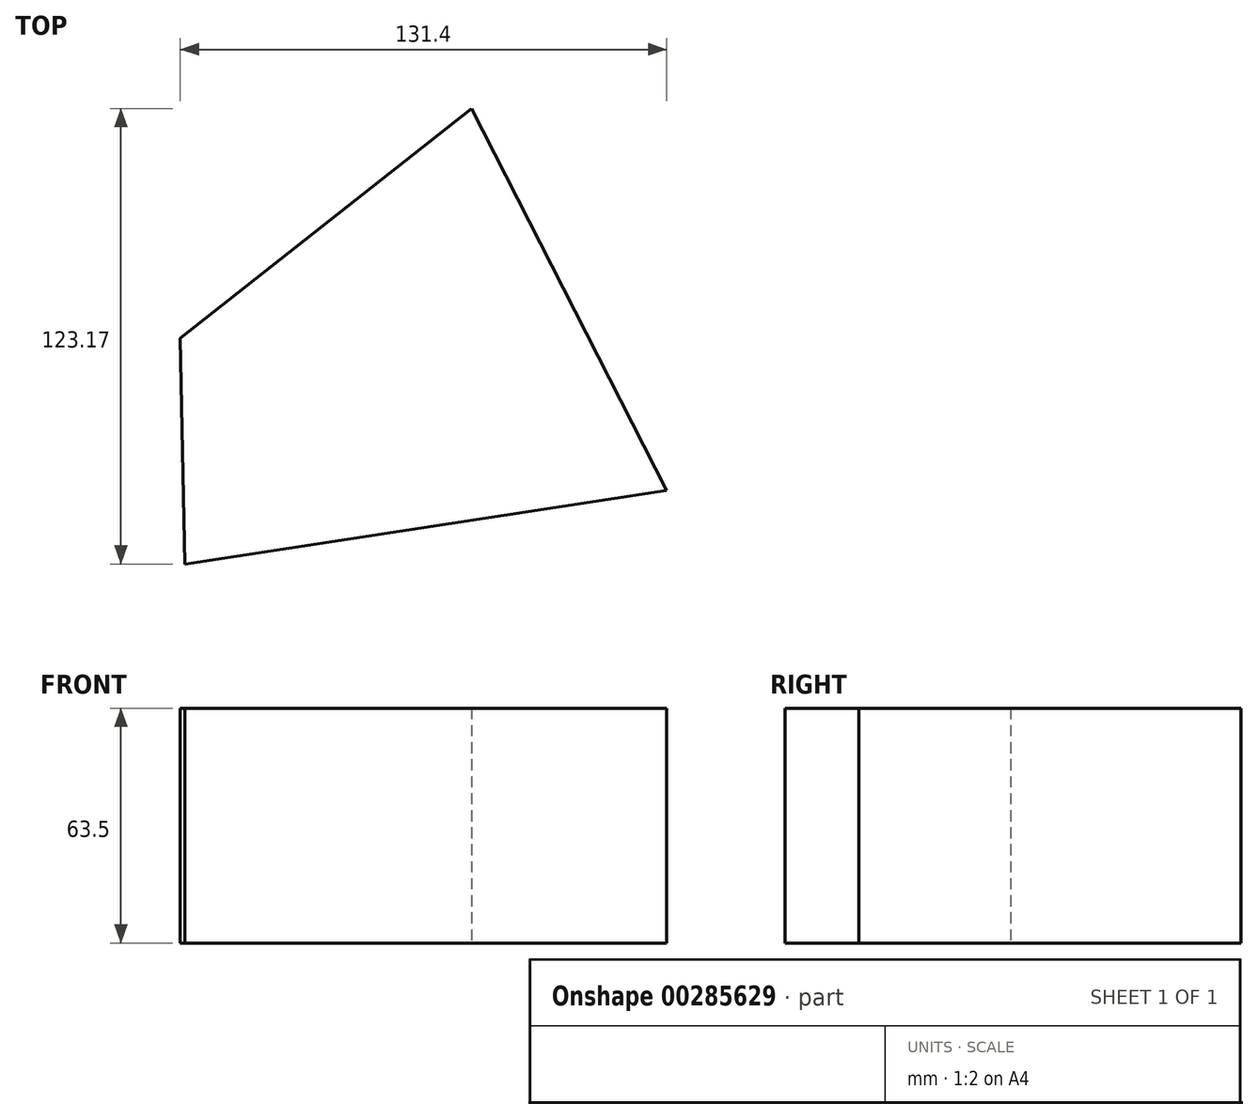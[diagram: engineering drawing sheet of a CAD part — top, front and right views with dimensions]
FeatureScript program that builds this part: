
annotation { "Feature Type Name" : "Feature", "Feature Type Description" : "" }
export const myFeature = defineFeature(function(context is Context, id is Id, definition is map)
    precondition{}
    {
        {
            var Q0;
            Q0=qCreatedBy(makeId("Top.planeOp"),FACE);
            var sketch = newSketch(context, id + "F0", { "sketchPlane" : qUnion([Q0])});
            skLineSegment(sketch, "E0", {"start": v(-57.79, -60.97) * mm, "end": v(72.36, -41.04) * mm});
            skLineSegment(sketch, "E1", {"start": v(72.36, -41.04) * mm, "end": v(19.66, 62.2) * mm});
            skLineSegment(sketch, "E2", {"start": v(19.66, 62.2) * mm, "end": v(-59.04, 0) * mm});
            skLineSegment(sketch, "E3", {"start": v(-57.79, -60.97) * mm, "end": v(-59.04, 0) * mm});
            skSolve(sketch);
        }
        {
            var Q0;
            Q0 = qSketchRegion(id + "F0", true);
            extrude(context, id + "F1", {"entities" : qUnion([Q0]), "depth" : 63.5 * mm});
        }
    });
